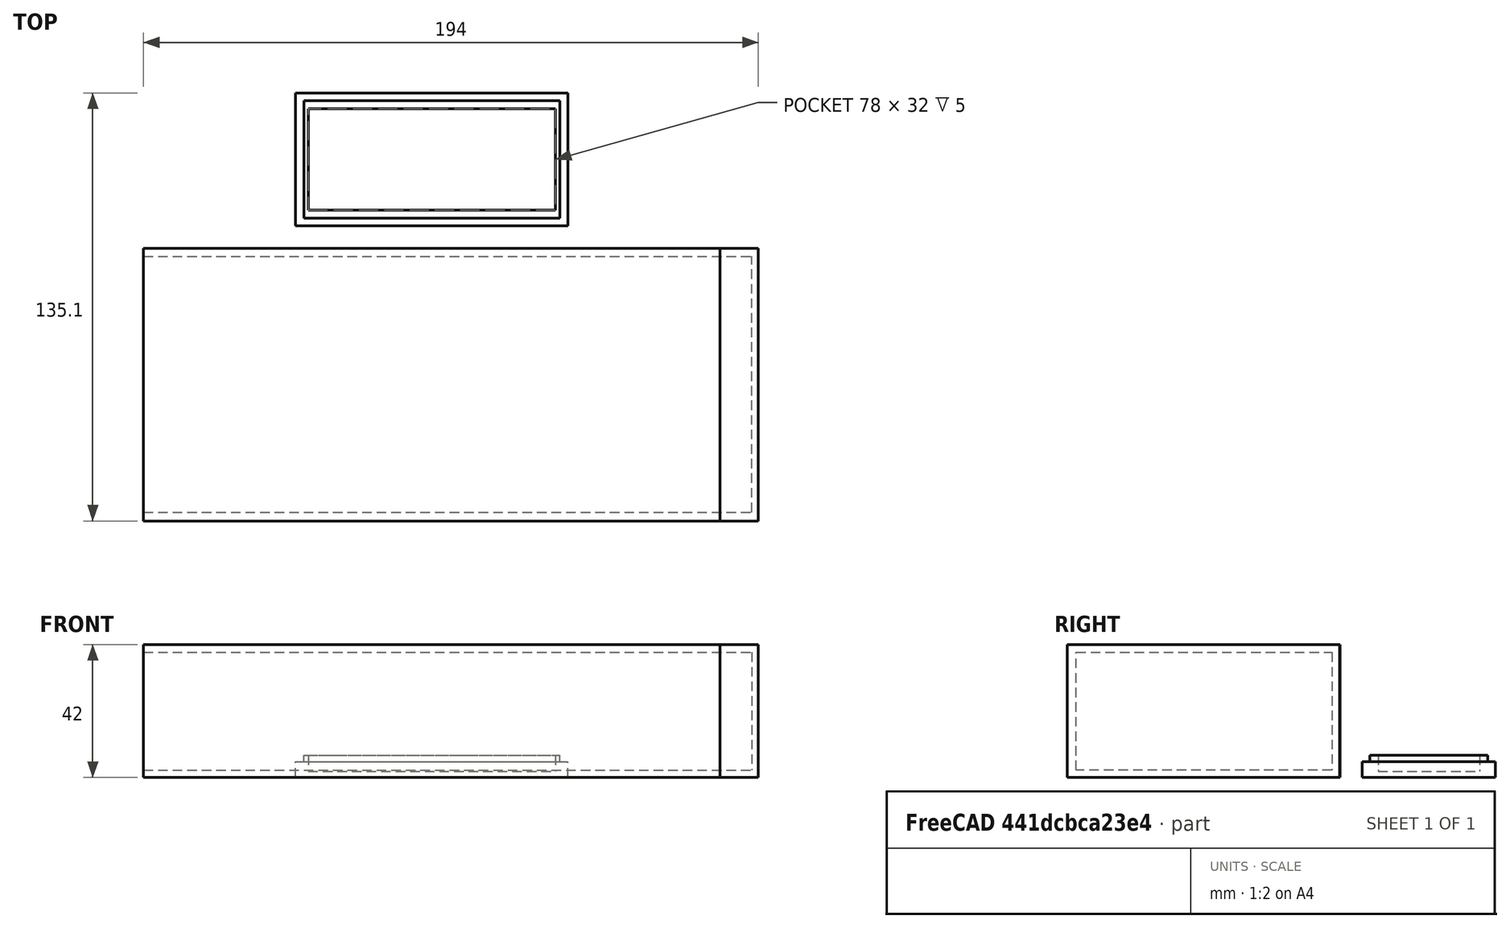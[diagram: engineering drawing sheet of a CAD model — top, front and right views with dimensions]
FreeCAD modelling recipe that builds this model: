
FCSTD DOCUMENT  (FreeCAD 1.0R39109 (Git))
Label: pylon_w_power
License: All rights reserved
LicenseURL: https://en.wikipedia.org/wiki/All_rights_reserved
objects: Sketcher::SketchObject×10, PartDesign::Pocket×6, PartDesign::Pad×4, PartDesign::Body×2, Assembly::JointGroup×1, Assembly::AssemblyObject×1, App::Part×1
note: 52 computed .brp shape members not serialized (recipe doc carries the construction recipe); baked Part::Feature solids carry a one-line shape summary decoded from their .brp

FEATURE [Sketcher::SketchObject] Sketch
  ArcFitTolerance = 1e-06
  AttachmentSupport = -> [XY_Plane]
  FullyConstrained = true
  MakeInternals = false
  MapMode = 5
  sketch-geometry (5):
    g0: LineSegment StartX=-91 StartY=-43 StartZ=0 EndX=91 EndY=-43 EndZ=0
    g1: LineSegment StartX=91 StartY=-43 StartZ=0 EndX=91 EndY=43 EndZ=0
    g2: LineSegment StartX=91 StartY=43 StartZ=0 EndX=-91 EndY=43 EndZ=0
    g3: LineSegment StartX=-91 StartY=43 StartZ=0 EndX=-91 EndY=-43 EndZ=0
    g4: GeomPoint [constr] X=0 Y=0 Z=0
  constraints (12):
    c: Coincident(g0,g1)
    c: Coincident(g1,g2)
    c: Coincident(g2,g3)
    c: Coincident(g3,g0)
    c: Horizontal(g0)
    c: Horizontal(g2)
    c: Vertical(g1)
    c: Vertical(g3)
    c: Symmetric(g2,g0,g4)
    c: Distance(g1,g3) = 182
    c: Distance(g0,g2) = 86
    c: Coincident(g4,g-1)
FEATURE [PartDesign::Pad] Pad
  Direction = (0,0,1)
  Length = 42
  Length2 = 10
  Profile = -> Sketch
  ReferenceAxis = -> Sketch [N_Axis]
  Refine = true
  Suppressed = false
  Type = 0
FEATURE [Sketcher::SketchObject] Sketch001
  ArcFitTolerance = 1e-06
  AttachmentSupport = -> [YZ_Plane]
  FullyConstrained = true
  MakeInternals = false
  MapMode = 5
  Placement = pos=(0,0,0) rot=(0.57735,0.57735,0.57735;2.0944rad)
FEATURE [Sketcher::SketchObject] Sketch002
  ArcFitTolerance = 1e-06
  AttachmentSupport = -> [Pad]
  FullyConstrained = false
  MakeInternals = false
  MapMode = 5
  Placement = pos=(-91,0,0) rot=(0.57735,-0.57735,-0.57735;2.0944rad)
  sketch-geometry (5):
    g0: LineSegment StartX=-38 StartY=4.98784 StartZ=0 EndX=38 EndY=4.98784 EndZ=0
    g1: LineSegment StartX=38 StartY=4.98784 StartZ=0 EndX=38 EndY=36.9878 EndZ=0
    g2: LineSegment StartX=38 StartY=36.9878 StartZ=0 EndX=-38 EndY=36.9878 EndZ=0
    g3: LineSegment StartX=-38 StartY=36.9878 StartZ=0 EndX=-38 EndY=4.98784 EndZ=0
    g4: GeomPoint [constr] X=1e-16 Y=20.9878 Z=0
  constraints (12):
    c: Coincident(g0,g1)
    c: Coincident(g1,g2)
    c: Coincident(g2,g3)
    c: Coincident(g3,g0)
    c: Horizontal(g0)
    c: Horizontal(g2)
    c: Vertical(g1)
    c: Vertical(g3)
    c: Symmetric(g2,g0,g4)
    c: Distance(g1,g3) = 76
    c: Distance(g0,g2) = 32
    c: PointOnObject(g4,g-2)
FEATURE [PartDesign::Pocket] Pocket
  BaseFeature = -> Pad
  Direction = (1,0,0)
  Length = 172
  Length2 = 5
  Profile = -> Sketch002
  ReferenceAxis = -> Sketch002 [N_Axis]
  Refine = true
  Suppressed = false
  Type = 0
FEATURE [Assembly::JointGroup] Joints
FEATURE [Assembly::AssemblyObject] Assembly
  Group = -> [Joints]
  Origin = -> Origin006
  Type = Assembly
FEATURE [Sketcher::SketchObject] Sketch003
  ArcFitTolerance = 1e-06
  AttachmentSupport = -> [XY_Plane]
  FullyConstrained = true
  MakeInternals = false
  MapMode = 5
FEATURE [Sketcher::SketchObject] Sketch007
  ArcFitTolerance = 1e-06
  AttachmentSupport = -> [Pocket]
  FullyConstrained = false
  MakeInternals = false
  MapMode = 5
  Placement = pos=(91,0,0) rot=(0.57735,0.57735,0.57735;2.0944rad)
  sketch-geometry (4):
    g0: LineSegment StartX=-42.9997 StartY=41.9991 StartZ=0 EndX=-42.9997 EndY=0 EndZ=0
    g1: LineSegment StartX=-42.9997 StartY=0 StartZ=0 EndX=42.9974 EndY=0 EndZ=0
    g2: LineSegment StartX=42.9974 StartY=0 StartZ=0 EndX=42.9974 EndY=41.9991 EndZ=0
    g3: LineSegment StartX=42.9974 StartY=41.9991 StartZ=0 EndX=-42.9997 EndY=41.9991 EndZ=0
  constraints (9):
    c: Coincident(g0,g1)
    c: Coincident(g1,g2)
    c: Coincident(g2,g3)
    c: Coincident(g3,g0)
    c: Vertical(g0)
    c: Vertical(g2)
    c: Horizontal(g1)
    c: Horizontal(g3)
    c: PointOnObject(g1,g-1)
FEATURE [PartDesign::Pad] Pad003
  BaseFeature = -> Pocket
  Direction = (1,0,0)
  Length = 12
  Length2 = 10
  Profile = -> Sketch007
  ReferenceAxis = -> Sketch007 [N_Axis]
  Refine = true
  Suppressed = false
  Type = 0
FEATURE [Sketcher::SketchObject] Sketch008
  ArcFitTolerance = 1e-06
  AttachmentSupport = -> [Pad003]
  FullyConstrained = false
  MakeInternals = false
  MapMode = 5
  Placement = pos=(81,0,0) rot=(0.57735,-0.57735,-0.57735;2.0944rad)
  sketch-geometry (4):
    g0: LineSegment StartX=-37.8741 StartY=36.8036 StartZ=0 EndX=-37.8741 EndY=5.03903 EndZ=0
    g1: LineSegment StartX=-37.8741 StartY=5.03903 StartZ=0 EndX=37.9514 EndY=5.03903 EndZ=0
    g2: LineSegment StartX=37.9514 StartY=5.03903 StartZ=0 EndX=37.9514 EndY=36.8036 EndZ=0
    g3: LineSegment StartX=37.9514 StartY=36.8036 StartZ=0 EndX=-37.8741 EndY=36.8036 EndZ=0
  constraints (8):
    c: Coincident(g0,g1)
    c: Coincident(g1,g2)
    c: Coincident(g2,g3)
    c: Coincident(g3,g0)
    c: Vertical(g0)
    c: Vertical(g2)
    c: Horizontal(g1)
    c: Horizontal(g3)
FEATURE [PartDesign::Pocket] Pocket002
  BaseFeature = -> Pad003
  Direction = (1,0,0)
  Length = 15
  Length2 = 5
  Profile = -> Sketch008
  ReferenceAxis = -> Sketch008 [N_Axis]
  Refine = true
  Suppressed = false
  Type = 0
FEATURE [Sketcher::SketchObject] Sketch009
  ArcFitTolerance = 1e-06
  AttachmentSupport = -> [Pocket002]
  FullyConstrained = false
  MakeInternals = false
  MapMode = 5
  Placement = pos=(-91,0,0) rot=(0.57735,-0.57735,-0.57735;2.0944rad)
  sketch-geometry (4):
    g0: LineSegment StartX=-40.5195 StartY=39.5025 StartZ=0 EndX=-40.5195 EndY=2.32773 EndZ=0
    g1: LineSegment StartX=-40.5195 StartY=2.32773 StartZ=0 EndX=40.2057 EndY=2.32773 EndZ=0
    g2: LineSegment StartX=40.2057 StartY=2.32773 StartZ=0 EndX=40.2057 EndY=39.5025 EndZ=0
    g3: LineSegment StartX=40.2057 StartY=39.5025 StartZ=0 EndX=-40.5195 EndY=39.5025 EndZ=0
  constraints (8):
    c: Coincident(g0,g1)
    c: Coincident(g1,g2)
    c: Coincident(g2,g3)
    c: Coincident(g3,g0)
    c: Vertical(g0)
    c: Vertical(g2)
    c: Horizontal(g1)
    c: Horizontal(g3)
FEATURE [PartDesign::Pocket] Pocket003
  BaseFeature = -> Pocket002
  Direction = (1,0,0)
  Length = 187
  Length2 = 5
  Profile = -> Sketch009
  ReferenceAxis = -> Sketch009 [N_Axis]
  Refine = true
  Suppressed = false
  Type = 0
FEATURE [PartDesign::Pocket] Pocket004
  BaseFeature = -> Pocket003
  Direction = (-1,0,0)
  Length = 4
  Length2 = 5
  Profile = -> Pocket003 [Edge31,Edge26,Edge30,Edge28]
  Refine = true
  Suppressed = false
  Type = 0
FEATURE [PartDesign::Pocket] Pocket005
  BaseFeature = -> Pocket004
  Direction = (1,0,0)
  Length = 5
  Length2 = 5
  Profile = -> Pocket004 [Face12]
  Refine = true
  Suppressed = false
  Type = 0
FEATURE [PartDesign::Body] Body
  AllowCompound = false
  Group = -> [Sketch,Pad,Sketch001,Sketch002,Pocket,Sketch003,Sketch007,Pad003,Sketch008,Pocket002,Sketch009,Pocket003,Pocket004,Pocket005]
  Origin = -> Origin
  Tip = -> Pocket005
FEATURE [App::Part] Part
  Group = -> [Body]
  Origin = -> Origin007
FEATURE [Sketcher::SketchObject] Sketch010
  ArcFitTolerance = 1e-06
  AttachmentSupport = -> [XY_Plane008]
  FullyConstrained = false
  MakeInternals = false
  MapMode = 5
  sketch-geometry (5):
    g0: LineSegment StartX=-43 StartY=50.1027 StartZ=0 EndX=43 EndY=50.1027 EndZ=0
    g1: LineSegment StartX=43 StartY=50.1027 StartZ=0 EndX=43 EndY=92.1027 EndZ=0
    g2: LineSegment StartX=43 StartY=92.1027 StartZ=0 EndX=-43 EndY=92.1027 EndZ=0
    g3: LineSegment StartX=-43 StartY=92.1027 StartZ=0 EndX=-43 EndY=50.1027 EndZ=0
    g4: GeomPoint [constr] X=0 Y=71.1027 Z=0
  constraints (12):
    c: Coincident(g0,g1)
    c: Coincident(g1,g2)
    c: Coincident(g2,g3)
    c: Coincident(g3,g0)
    c: Horizontal(g0)
    c: Horizontal(g2)
    c: Vertical(g1)
    c: Vertical(g3)
    c: Symmetric(g2,g0,g4)
    c: Distance(g1,g3) = 86
    c: Distance(g0,g2) = 42
    c: PointOnObject(g4,g-2)
FEATURE [PartDesign::Pad] Pad004
  Direction = (0,0,1)
  Length = 5
  Length2 = 10
  Profile = -> Sketch010
  ReferenceAxis = -> Sketch010 [N_Axis]
  Refine = true
  Suppressed = false
  Type = 0
FEATURE [Sketcher::SketchObject] Sketch012
  ArcFitTolerance = 1e-06
  AttachmentSupport = -> [Pad004]
  FullyConstrained = false
  MakeInternals = false
  MapMode = 5
  Placement = pos=(0,0,5) rot=(0,0,1;0rad)
  sketch-geometry (5):
    g0: LineSegment StartX=-40.365 StartY=52.5172 StartZ=0 EndX=40.365 EndY=52.5172 EndZ=0
    g1: LineSegment StartX=40.365 StartY=52.5172 StartZ=0 EndX=40.365 EndY=89.6872 EndZ=0
    g2: LineSegment StartX=40.365 StartY=89.6872 StartZ=0 EndX=-40.365 EndY=89.6872 EndZ=0
    g3: LineSegment StartX=-40.365 StartY=89.6872 StartZ=0 EndX=-40.365 EndY=52.5172 EndZ=0
    g4: GeomPoint [constr] X=0 Y=71.1022 Z=0
  constraints (12):
    c: Coincident(g0,g1)
    c: Coincident(g1,g2)
    c: Coincident(g2,g3)
    c: Coincident(g3,g0)
    c: Horizontal(g0)
    c: Horizontal(g2)
    c: Vertical(g1)
    c: Vertical(g3)
    c: Symmetric(g2,g0,g4)
    c: Distance(g1,g3) = 80.73
    c: Distance(g0,g2) = 37.17
    c: PointOnObject(g4,g-2)
FEATURE [PartDesign::Pad] Pad005
  BaseFeature = -> Pad004
  Direction = (0,0,1)
  Length = 2
  Length2 = 10
  Profile = -> Sketch012
  ReferenceAxis = -> Sketch012 [N_Axis]
  Refine = true
  Suppressed = false
  Type = 0
FEATURE [Sketcher::SketchObject] Sketch013
  ArcFitTolerance = 1e-06
  AttachmentSupport = -> [Pad005]
  FullyConstrained = false
  MakeInternals = false
  MapMode = 5
  Placement = pos=(0,0,7) rot=(0,0,1;0rad)
  sketch-geometry (5):
    g0: LineSegment StartX=-39 StartY=55.0963 StartZ=0 EndX=39 EndY=55.0963 EndZ=0
    g1: LineSegment StartX=39 StartY=55.0963 StartZ=0 EndX=39 EndY=87.0963 EndZ=0
    g2: LineSegment StartX=39 StartY=87.0963 StartZ=0 EndX=-39 EndY=87.0963 EndZ=0
    g3: LineSegment StartX=-39 StartY=87.0963 StartZ=0 EndX=-39 EndY=55.0963 EndZ=0
    g4: GeomPoint [constr] X=0 Y=71.0963 Z=0
  constraints (12):
    c: Coincident(g0,g1)
    c: Coincident(g1,g2)
    c: Coincident(g2,g3)
    c: Coincident(g3,g0)
    c: Horizontal(g0)
    c: Horizontal(g2)
    c: Vertical(g1)
    c: Vertical(g3)
    c: Symmetric(g2,g0,g4)
    c: Distance(g1,g3) = 78
    c: Distance(g0,g2) = 32
    c: PointOnObject(g4,g-2)
FEATURE [PartDesign::Pocket] Pocket006
  BaseFeature = -> Pad005
  Direction = (0,0,-1)
  Length = 5
  Length2 = 5
  Profile = -> Sketch013
  ReferenceAxis = -> Sketch013 [N_Axis]
  Refine = true
  Suppressed = false
  Type = 0
FEATURE [PartDesign::Body] Body001
  AllowCompound = false
  Group = -> [Sketch010,Pad004,Sketch012,Pad005,Sketch013,Pocket006]
  Origin = -> Origin008
  Tip = -> Pocket006
